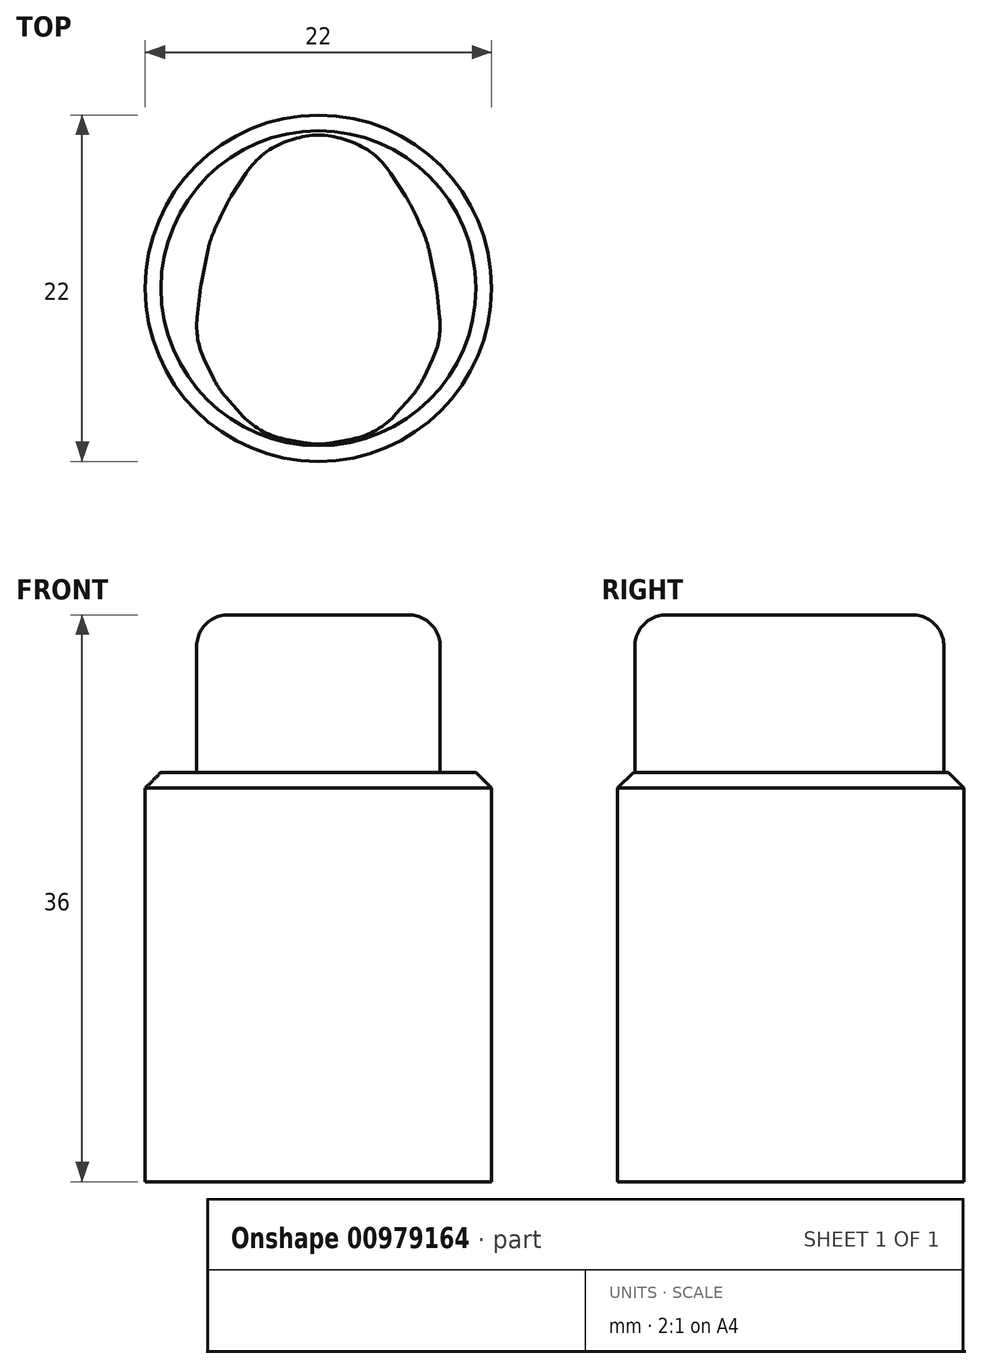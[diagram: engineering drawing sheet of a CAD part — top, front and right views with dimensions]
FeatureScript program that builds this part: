
annotation { "Feature Type Name" : "Feature", "Feature Type Description" : "" }
export const myFeature = defineFeature(function(context is Context, id is Id, definition is map)
    precondition{}
    {
        {
            var Q0;
            Q0=qCreatedBy(makeId("Top.planeOp"),FACE);
            var sketch = newSketch(context, id + "F0", { "sketchPlane" : qUnion([Q0])});
            skLineSegment(sketch, "E0", {"start": v(0, 10) * mm, "end": v(0, -10) * mm});
            skLineSegment(sketch, "E1", {"start": v(-7.5, 0) * mm, "end": v(7.5, 0) * mm});
            skLineSegment(sketch, "E2", {"start": v(0, 0) * mm, "end": v(6.36, -6.36) * mm});
            skLineSegment(sketch, "E3", {"start": v(0, 0) * mm, "end": v(5.66, 5.66) * mm});
            skLineSegment(sketch, "E4", {"start": v(0, 0) * mm, "end": v(7.85, -3.25) * mm});
            skLineSegment(sketch, "E5", {"start": v(0, 0) * mm, "end": v(3.83, -9.24) * mm});
            skLineSegment(sketch, "E6", {"start": v(0, 0) * mm, "end": v(6.93, 2.87) * mm});
            skLineSegment(sketch, "E7", {"start": v(0, 0) * mm, "end": v(3.64, 8.78) * mm});
            skLineSegment(sketch, "E8", {"start": v(0, -10) * mm, "end": v(3.83, -9.24) * mm});
            skLineSegment(sketch, "E9", {"start": v(6.36, -6.36) * mm, "end": v(3.83, -9.24) * mm});
            skLineSegment(sketch, "E10", {"start": v(7.85, -3.25) * mm, "end": v(6.36, -6.36) * mm});
            skLineSegment(sketch, "E11", {"start": v(7.5, 0) * mm, "end": v(7.85, -3.25) * mm});
            skLineSegment(sketch, "E12", {"start": v(6.93, 2.87) * mm, "end": v(7.5, 0) * mm});
            skLineSegment(sketch, "E13", {"start": v(5.66, 5.66) * mm, "end": v(6.93, 2.87) * mm});
            skLineSegment(sketch, "E14", {"start": v(3.64, 8.78) * mm, "end": v(5.66, 5.66) * mm});
            skLineSegment(sketch, "E15", {"start": v(0, 10) * mm, "end": v(3.64, 8.78) * mm});
            skSolve(sketch);
        }
        {
            var Q0;
            Q0=qCreatedBy(makeId("Top.planeOp"),FACE);
            var sketch = newSketch(context, id + "F1", { "sketchPlane" : qUnion([Q0])});
            skLineSegment(sketch, "E16", {"start": v(1.6, 9.46) * mm, "end": v(1.98, 9.33) * mm});
            skLineSegment(sketch, "E17", {"start": v(4.58, 7.31) * mm, "end": v(5.54, 5.84) * mm});
            skLineSegment(sketch, "E18", {"start": v(7.02, 2.44) * mm, "end": v(7.46, 0.22) * mm});
            skLineSegment(sketch, "E19", {"start": v(7.52, -0.22) * mm, "end": v(7.7, -1.87) * mm});
            skLineSegment(sketch, "E20", {"start": v(7.25, -4.51) * mm, "end": v(6.66, -5.74) * mm});
            skLineSegment(sketch, "E21", {"start": v(5.9, -6.89) * mm, "end": v(4.94, -7.97) * mm});
            skLineSegment(sketch, "E22", {"start": v(2.17, -9.57) * mm, "end": v(0.98, -9.8) * mm});
            skArc(sketch, "E23", {"start": v(6.75, 3.33) * mm, "mid": v(6.29, 4.4) * mm, "end": v(5.77, 5.44) * mm});
            skPoint(sketch, "E24.visualSharp", {"position": v(3.64, 8.78) * mm});
            skArc(sketch, "E24.filletArc", {"start": v(4.58, 7.31) * mm, "mid": v(3.45, 8.54) * mm, "end": v(1.98, 9.33) * mm});
            skPoint(sketch, "E25.visualSharp", {"position": v(5.66, 5.66) * mm});
            skArc(sketch, "E25.filletArc", {"start": v(5.77, 5.44) * mm, "mid": v(5.66, 5.64) * mm, "end": v(5.54, 5.84) * mm});
            skPoint(sketch, "E26.visualSharp", {"position": v(6.93, 2.87) * mm});
            skArc(sketch, "E26.filletArc", {"start": v(7.02, 2.44) * mm, "mid": v(6.9, 2.9) * mm, "end": v(6.75, 3.33) * mm});
            skPoint(sketch, "E27.visualSharp", {"position": v(7.5, 0) * mm});
            skArc(sketch, "E27.filletArc", {"start": v(7.52, -0.22) * mm, "mid": v(7.5, 0) * mm, "end": v(7.46, 0.22) * mm});
            skPoint(sketch, "E28.visualSharp", {"position": v(7.85, -3.25) * mm});
            skArc(sketch, "E28.filletArc", {"start": v(7.25, -4.51) * mm, "mid": v(7.66, -3.22) * mm, "end": v(7.7, -1.87) * mm});
            skPoint(sketch, "E29.visualSharp", {"position": v(6.36, -6.36) * mm});
            skArc(sketch, "E29.filletArc", {"start": v(5.9, -6.89) * mm, "mid": v(6.32, -6.34) * mm, "end": v(6.66, -5.74) * mm});
            skPoint(sketch, "E30.visualSharp", {"position": v(3.83, -9.24) * mm});
            skArc(sketch, "E30.filletArc", {"start": v(2.17, -9.57) * mm, "mid": v(3.69, -9) * mm, "end": v(4.94, -7.97) * mm});
            skArc(sketch, "E31.MirrorCS", {"start": v(-7.52, -0.22) * mm, "mid": v(-7.5, 0) * mm, "end": v(-7.46, 0.22) * mm});
            skArc(sketch, "E32.MirrorCS", {"start": v(-5.77, 5.44) * mm, "mid": v(-5.66, 5.64) * mm, "end": v(-5.54, 5.84) * mm});
            skArc(sketch, "E33.MirrorCS", {"start": v(-7.02, 2.44) * mm, "mid": v(-6.9, 2.9) * mm, "end": v(-6.75, 3.33) * mm});
            skArc(sketch, "E34.MirrorCS", {"start": v(-5.9, -6.89) * mm, "mid": v(-6.32, -6.34) * mm, "end": v(-6.66, -5.74) * mm});
            skPoint(sketch, "E35.MirrorP", {"position": v(-5.66, 5.66) * mm});
            skArc(sketch, "E36.MirrorCS", {"start": v(-4.58, 7.31) * mm, "mid": v(-3.45, 8.54) * mm, "end": v(-1.98, 9.33) * mm});
            skArc(sketch, "E37.MirrorCS", {"start": v(-7.25, -4.51) * mm, "mid": v(-7.66, -3.22) * mm, "end": v(-7.7, -1.87) * mm});
            skPoint(sketch, "E38.MirrorP", {"position": v(-6.36, -6.36) * mm});
            skPoint(sketch, "E39.MirrorP", {"position": v(-7.85, -3.25) * mm});
            skLineSegment(sketch, "E40.MirrorCS", {"start": v(-1.6, 9.46) * mm, "end": v(-1.98, 9.33) * mm});
            skPoint(sketch, "E41.MirrorP", {"position": v(-7.5, 0) * mm});
            skPoint(sketch, "E42.MirrorP", {"position": v(-3.64, 8.78) * mm});
            skPoint(sketch, "E43.MirrorP", {"position": v(-6.93, 2.87) * mm});
            skPoint(sketch, "E44.MirrorP", {"position": v(-3.83, -9.24) * mm});
            skLineSegment(sketch, "E45.MirrorCS", {"start": v(-7.25, -4.51) * mm, "end": v(-6.66, -5.74) * mm});
            skLineSegment(sketch, "E46.MirrorCS", {"start": v(-2.17, -9.57) * mm, "end": v(-0.98, -9.8) * mm});
            skLineSegment(sketch, "E47.MirrorCS", {"start": v(-4.58, 7.31) * mm, "end": v(-5.54, 5.84) * mm});
            skLineSegment(sketch, "E48.MirrorCS", {"start": v(-7.52, -0.22) * mm, "end": v(-7.7, -1.87) * mm});
            skArc(sketch, "E49.MirrorCS", {"start": v(-2.17, -9.57) * mm, "mid": v(-3.69, -9) * mm, "end": v(-4.94, -7.97) * mm});
            skLineSegment(sketch, "E50.MirrorCS", {"start": v(-7.02, 2.44) * mm, "end": v(-7.46, 0.22) * mm});
            skLineSegment(sketch, "E51.MirrorCS", {"start": v(-5.9, -6.89) * mm, "end": v(-4.94, -7.97) * mm});
            skArc(sketch, "E52.MirrorCS", {"start": v(-6.75, 3.33) * mm, "mid": v(-6.29, 4.4) * mm, "end": v(-5.77, 5.44) * mm});
            skPoint(sketch, "E53.visualSharp", {"position": v(0, 10) * mm});
            skArc(sketch, "E53.filletArc", {"start": v(1.6, 9.46) * mm, "mid": v(0, 9.72) * mm, "end": v(-1.6, 9.46) * mm});
            skPoint(sketch, "E54.visualSharp", {"position": v(0, -10) * mm});
            skArc(sketch, "E54.filletArc", {"start": v(-0.98, -9.8) * mm, "mid": v(0, -9.9) * mm, "end": v(0.98, -9.8) * mm});
            skSolve(sketch);
        }
        {
            var Q0;
            Q0 = qSketchRegion(id + "F1", true);
            extrude(context, id + "F2", {"entities" : qUnion([Q0]), "depth" : 36 * mm, "offsetDistance" : 25 * mm});
        }
        {
            var Q0;
            Q0=makeQuery(id+"F2.opExtrude","CAP_EDGE",EDGE,{"disambiguationData":[OSD([sQuery(id+"F1.wireOp",EDGE,"E30.filletArc")])],"isStart":false});
            fillet(context, id + "F3", {"entities" : qUnion([Q0]), "radius" : 2 * mm, "tangentPropagation" : true, "allowEdgeOverflow" : false});
        }
        {
            var Q0;
            Q0=makeQuery(id+"F2.opExtrude","CAP_FACE",FACE,{"disambiguationData":[OSD([sQuery(id+"F1.wireOp",EDGE,"E16"),sQuery(id+"F1.wireOp",EDGE,"E17"),sQuery(id+"F1.wireOp",EDGE,"E18"),sQuery(id+"F1.wireOp",EDGE,"E19"),sQuery(id+"F1.wireOp",EDGE,"E20"),sQuery(id+"F1.wireOp",EDGE,"E21"),sQuery(id+"F1.wireOp",EDGE,"E22"),sQuery(id+"F1.wireOp",EDGE,"E23"),sQuery(id+"F1.wireOp",EDGE,"E24.filletArc"),sQuery(id+"F1.wireOp",EDGE,"E25.filletArc"),sQuery(id+"F1.wireOp",EDGE,"E26.filletArc"),sQuery(id+"F1.wireOp",EDGE,"E27.filletArc"),sQuery(id+"F1.wireOp",EDGE,"E28.filletArc"),sQuery(id+"F1.wireOp",EDGE,"E29.filletArc"),sQuery(id+"F1.wireOp",EDGE,"E30.filletArc"),sQuery(id+"F1.wireOp",EDGE,"E31.MirrorCS"),sQuery(id+"F1.wireOp",EDGE,"E32.MirrorCS"),sQuery(id+"F1.wireOp",EDGE,"E33.MirrorCS"),sQuery(id+"F1.wireOp",EDGE,"E34.MirrorCS"),sQuery(id+"F1.wireOp",EDGE,"E36.MirrorCS"),sQuery(id+"F1.wireOp",EDGE,"E37.MirrorCS"),sQuery(id+"F1.wireOp",EDGE,"E40.MirrorCS"),sQuery(id+"F1.wireOp",EDGE,"E45.MirrorCS"),sQuery(id+"F1.wireOp",EDGE,"E46.MirrorCS"),sQuery(id+"F1.wireOp",EDGE,"E47.MirrorCS"),sQuery(id+"F1.wireOp",EDGE,"E48.MirrorCS"),sQuery(id+"F1.wireOp",EDGE,"E49.MirrorCS"),sQuery(id+"F1.wireOp",EDGE,"E50.MirrorCS"),sQuery(id+"F1.wireOp",EDGE,"E51.MirrorCS"),sQuery(id+"F1.wireOp",EDGE,"E52.MirrorCS"),sQuery(id+"F1.wireOp",EDGE,"E53.filletArc"),sQuery(id+"F1.wireOp",EDGE,"E54.filletArc")])],"isStart":true});
            var sketch = newSketch(context, id + "F4", { "sketchPlane" : qUnion([Q0])});
            skCircle(sketch, "E55", {"center": v(0, 0) * mm, "radius": 11 * mm});
            skSolve(sketch);
        }
        {
            var Q0;
            Q0=makeQuery(id+"F4.imprint","IMPRINT",FACE,{"disambiguationData":[TD([[makeQuery(id+"F4.imprint","IMPRINT",EDGE,{"derivedFrom":sQuery(id+"F4.wireOp",EDGE,"E55")}),1.0]])]});
            extrude(context, id + "F5", {"entities" : qUnion([Q0]), "operationType" : NewBodyOperationType.ADD, "oppositeDirection" : true, "depth" : 26 * mm, "offsetDistance" : 25 * mm});
        }
        {
            var Q0;
            Q0=makeQuery(id+"F5.opExtrude","CAP_EDGE",EDGE,{"disambiguationData":[OSD([sQuery(id+"F4.wireOp",EDGE,"E55")])],"isStart":false});
            chamfer(context, id + "F6", {"entities" : qUnion([Q0]), "width" : 1 * mm, "tangentPropagation" : true});
        }
    });
